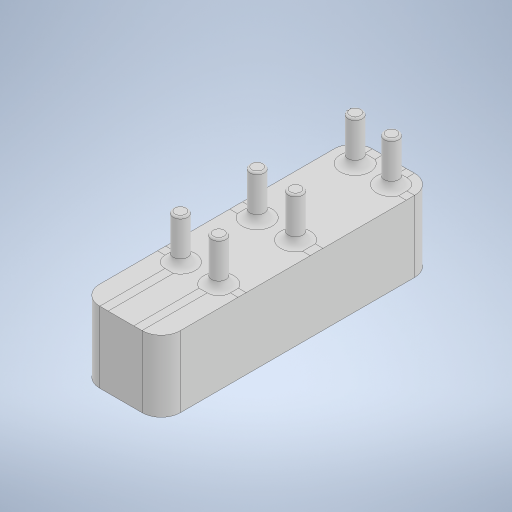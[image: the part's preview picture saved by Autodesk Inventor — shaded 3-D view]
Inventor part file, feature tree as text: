
AUTODESK INVENTOR PART (.ipt)
format: ipt  version: 2024.1 (Build 281209000, 209)  size: 987,648 bytes
history: native  units: in
note: dims shown in document units (in); Inventor stores cm internally (conversion verified against a paired STEP export)
features: sketch x6, extrude x5, fillet x4, thicken_offset x4, move_body x3, direct_edit x2, other x2
ambient origin geometry x8: Origin, YZ Plane, XZ Plane, XY Plane, X Axis, Y Axis, Z Axis, Center Point
bodies: Solid1 (feature_tree)
feature tree (26):
  extrude  "Extrusion1"  Depth=1.1811in
  extrude  "Extrusion2"  Depth=0.0787in
  extrude  "Extrusion3"  Depth=1.5748in
  extrude  "Extrusion4"  Depth=1.969in
  fillet  "Fillet4"  Radius=1.969in
  direct_edit  "Direct Edit1"
  direct_edit  "Direct Edit2"
  fillet  "Fillet3"  Radius=0.3935in
  thicken_offset  "Thicken1"
  fillet  "Fillet5"  Radius=0.3935in
  other  "Direct Edit4_v4.4"
  sketch  "Sketch5"  dims[d12=0.2953in d13=0.2953in d14=0.2953in]
  extrude  "Extrusion6"  Depth=0.2953in
  other  "v4.5"
  fillet  "Fillet6"  Radius=0.2953in
  thicken_offset  "Thicken2"
  thicken_offset  "Thicken3"
  thicken_offset  "Thicken4"
  sketch  "Sketch8"  dims[d15=0.2953in d16=0.2953in d17=0.2953in d18=0.1575in d19=0.1575in d20=0.1575in d21=0.1575in d22=0.1575in d23=0.1575in d24=0.5512in d25=0.0in d26=0.5512in d27=0.0in d28=0.2756in d29=0.0394in d30=0.0in d33=0.0in d34=0.0in d35=1.9685in d36=0.0in d37=0.0in d38=1.378in d39=0.1575in d40=0.0394in d42=0.0787in d43=0.0394in d44=0.1575in d45=0.1181in d46=0.0in d47=0.0787in d48=0.2362in d49=0.0in d55=0.0in d56=0.0in d57=-0.2362in d58=0.125in d62=0.7459in d63=0.0394in d64=0.0394in d65=0.0394in d66=0.125in d67=0.7874in d74=0.1575in d75=0.1575in d76=1.1811in d77=0.1575in d31=0.5in d32=0.0344in]
  sketch  "Sketch1"  dims[d0=3.937in d1=1.1811in]
  sketch  "Sketch2"  dims[d2=0.0787in d3=0.0in d4=0.1969in]
  sketch  "Sketch3"  dims[d5=0.1969in d6=1.5748in]
  sketch  "Sketch4"  dims[d7=1.5748in d8=1.969in d9=1.969in d10=0.3935in d11=0.3935in]
  move_body  "Move1"
  move_body  "Move2"
  move_body  "Move4"
